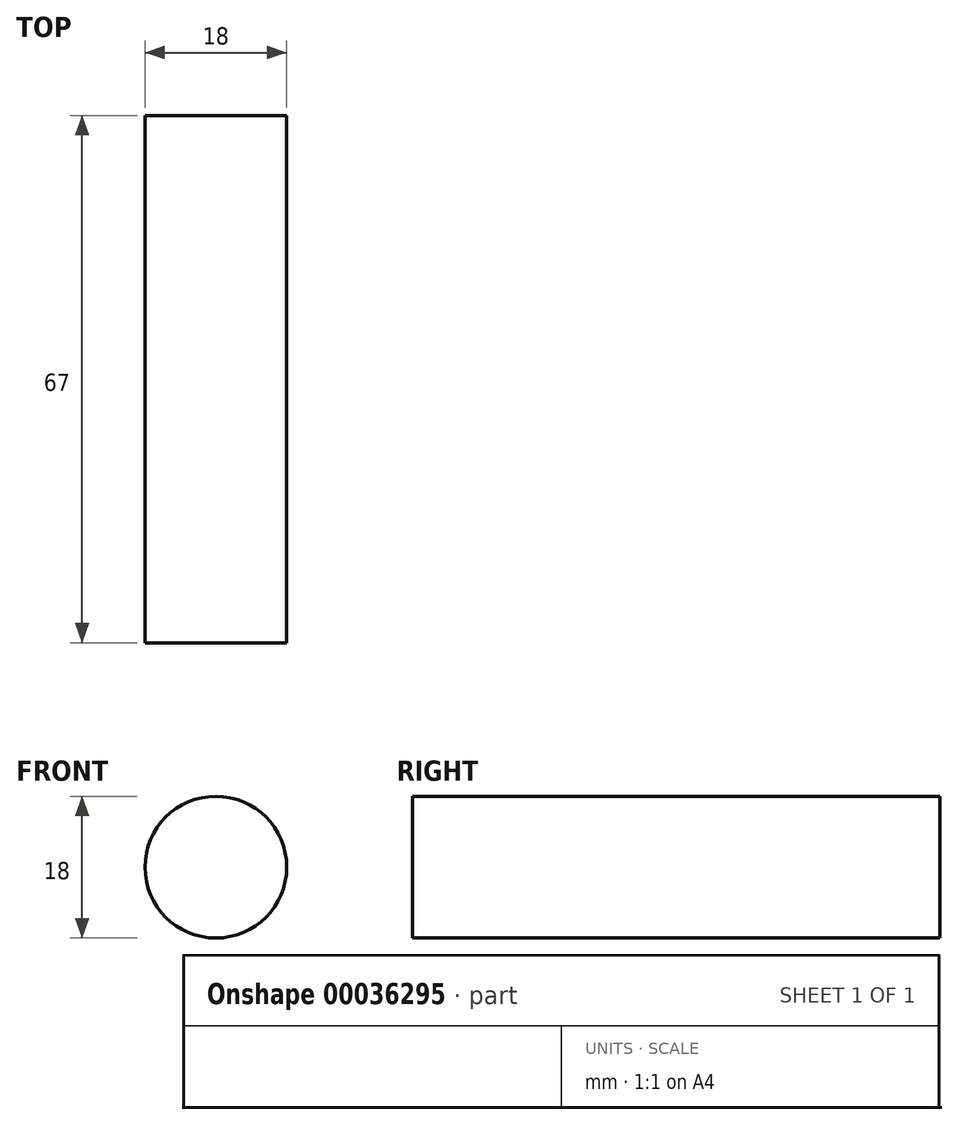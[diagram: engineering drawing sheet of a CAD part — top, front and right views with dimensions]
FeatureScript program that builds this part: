
annotation { "Feature Type Name" : "Feature", "Feature Type Description" : "" }
export const myFeature = defineFeature(function(context is Context, id is Id, definition is map)
    precondition{}
    {
        {
            var Q0;
            Q0=qCreatedBy(makeId("Front.planeOp"),FACE);
            var sketch = newSketch(context, id + "F0", { "sketchPlane" : qUnion([Q0])});
            skCircle(sketch, "E0", {"center": v(0, 0) * mm, "radius": 9 * mm});
            skSolve(sketch);
        }
        {
            var Q0;
            Q0=makeQuery(id+"F0.imprint","IMPRINT",FACE,{"disambiguationData":[TD([[makeQuery(id+"F0.imprint","IMPRINT",EDGE,{"derivedFrom":sQuery(id+"F0.wireOp",EDGE,"E0")}),1.0]])]});
            extrude(context, id + "F1", {"entities" : qUnion([Q0]), "depth" : 67 * mm});
        }
    });
